# Revit family: Winkelkonsole mit 2 Streben 200x200x 5, VA
name_source: partatom
category: HLS-Bauteile
revit_build: Autodesk Revit 2017 (Build: 20190507_1515(x64)
units: mm (PartAtom-declared; Revit-internal decimal feet)

## family parameters
Basisbauteil = Fläche
Beim Laden mit Abzugskörper schneiden = Nein
Bemaßung runder Anschluss = Durchmesser verwenden
Gemeinsam genutzt = Ja
Raumberechnungspunkt = Nein
Teiletyp = Normal

## types (2) — shared parameters
Abmessung = 200 x 200 x 5 mm
Fabrikat = MEFA
Firma = MEFA Befestigungs- und Montagesysteme GmbH
Gewicht = 1.37 kg
Gewicht pro Bauteil = 1.37 kg
Höhe = 200 mm
Kurztext2 = 200 x 200 x 5 mm für Profil 45
L = 200 mm  [stored 0.656168 ft]
Last bei Länge = 120 mm
Länge = 200 mm  [stored 0.656168 ft]
Material = Edelstahl
Mengeneinheit = St
Profiltyp = 45
Stärke = 5 mm  [stored 0.0164042 ft]
Vorgabe-Ansicht = 1219 mm
max. zul. Last F1 = 0.00 kip
max. zul. Last F2 = 0.00 kip
vpe = 1 St

## per-type parameters (varying)
| type | Artikelnummer | EAN | Kurztext1 | Materialname |
| Winkelkonsole mit 2 Streben 200x200x 5, V2A | 0480408 | 4250928412690 | Winkelkonsole mit 2 Streben V2A | V2A |
| Winkelkonsole mit 2 Streben 200x200x 5, V4A | 0481408 | 4250928413017 | Winkelkonsole mit 2 Streben V4A | V4A |

note: [stored X ft] marks values corroborated as IEEE doubles in the binary element streams (Revit-internal decimal feet)
